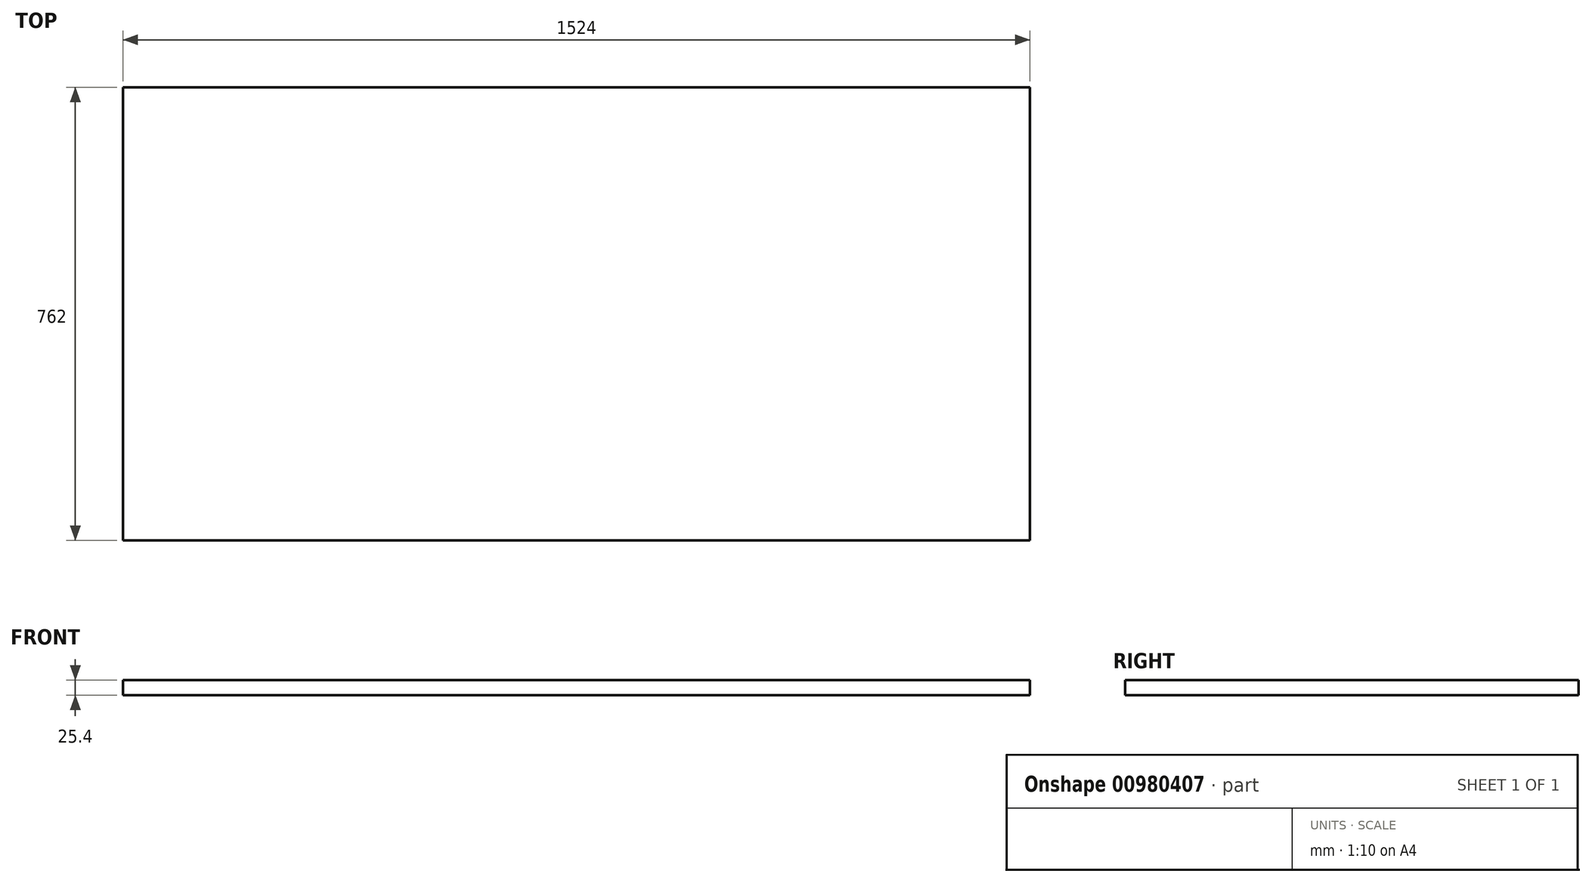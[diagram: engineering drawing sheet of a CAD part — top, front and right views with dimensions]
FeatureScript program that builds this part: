
annotation { "Feature Type Name" : "Feature", "Feature Type Description" : "" }
export const myFeature = defineFeature(function(context is Context, id is Id, definition is map)
    precondition{}
    {
        {
            var Q0;
            Q0=qCreatedBy(makeId("Top.planeOp"),FACE);
            var sketch = newSketch(context, id + "F0", { "sketchPlane" : qUnion([Q0])});
            skLineSegment(sketch, "E0.bottom", {"start": v(762, -381) * mm, "end": v(-762, -381) * mm});
            skLineSegment(sketch, "E0.top", {"start": v(762, 381) * mm, "end": v(-762, 381) * mm});
            skLineSegment(sketch, "E0.left", {"start": v(762, -381) * mm, "end": v(762, 381) * mm});
            skLineSegment(sketch, "E0.right", {"start": v(-762, -381) * mm, "end": v(-762, 381) * mm});
            skSolve(sketch);
        }
        {
            var Q0;
            Q0 = qSketchRegion(id + "F0", true);
            extrude(context, id + "F1", {"entities" : qUnion([Q0]), "depth" : 25.4 * mm, "offsetDistance" : 25.4 * mm});
        }
    });
